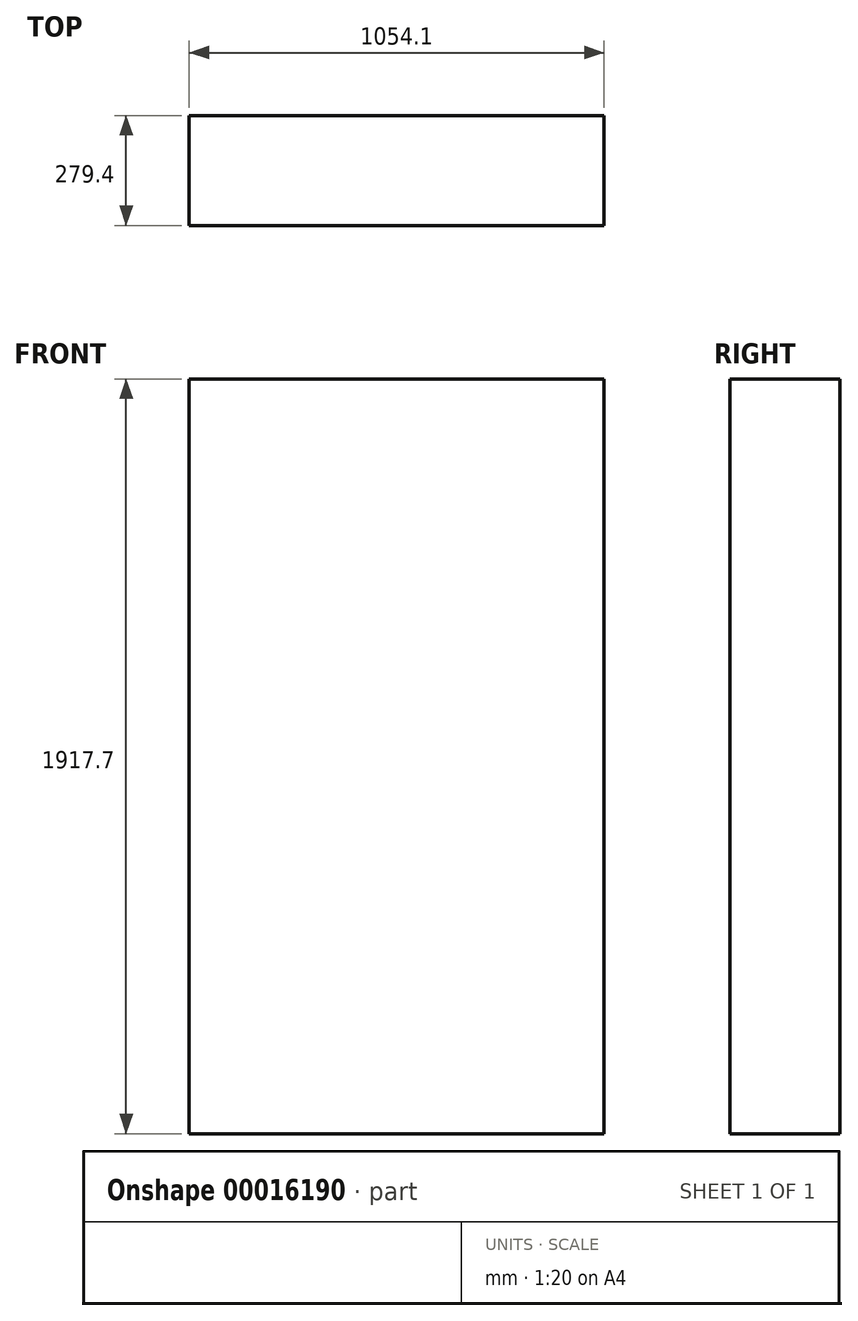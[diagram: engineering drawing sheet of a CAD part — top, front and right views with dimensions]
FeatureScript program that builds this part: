
annotation { "Feature Type Name" : "Feature", "Feature Type Description" : "" }
export const myFeature = defineFeature(function(context is Context, id is Id, definition is map)
    precondition{}
    {
        {
            var Q0;
            Q0=qCreatedBy(makeId("Top.planeOp"),FACE);
            var sketch = newSketch(context, id + "F0", { "sketchPlane" : qUnion([Q0])});
            skLineSegment(sketch, "E0.rect.bottom", {"start": v(527.05, 139.7) * mm, "end": v(-527.05, 139.7) * mm});
            skLineSegment(sketch, "E0.rect.top", {"start": v(527.05, -139.7) * mm, "end": v(-527.05, -139.7) * mm});
            skLineSegment(sketch, "E0.rect.left", {"start": v(527.05, 139.7) * mm, "end": v(527.05, -139.7) * mm});
            skLineSegment(sketch, "E0.rect.right", {"start": v(-527.05, 139.7) * mm, "end": v(-527.05, -139.7) * mm});
            skPoint(sketch, "E0.rect.middle", {"position": v(0, 0) * mm});
            skSolve(sketch);
        }
        {
            var Q0;
            Q0 = qSketchRegion(id + "F0", true);
            extrude(context, id + "F1", {"entities" : qUnion([Q0]), "depth" : 1917.7 * mm});
        }
    });
